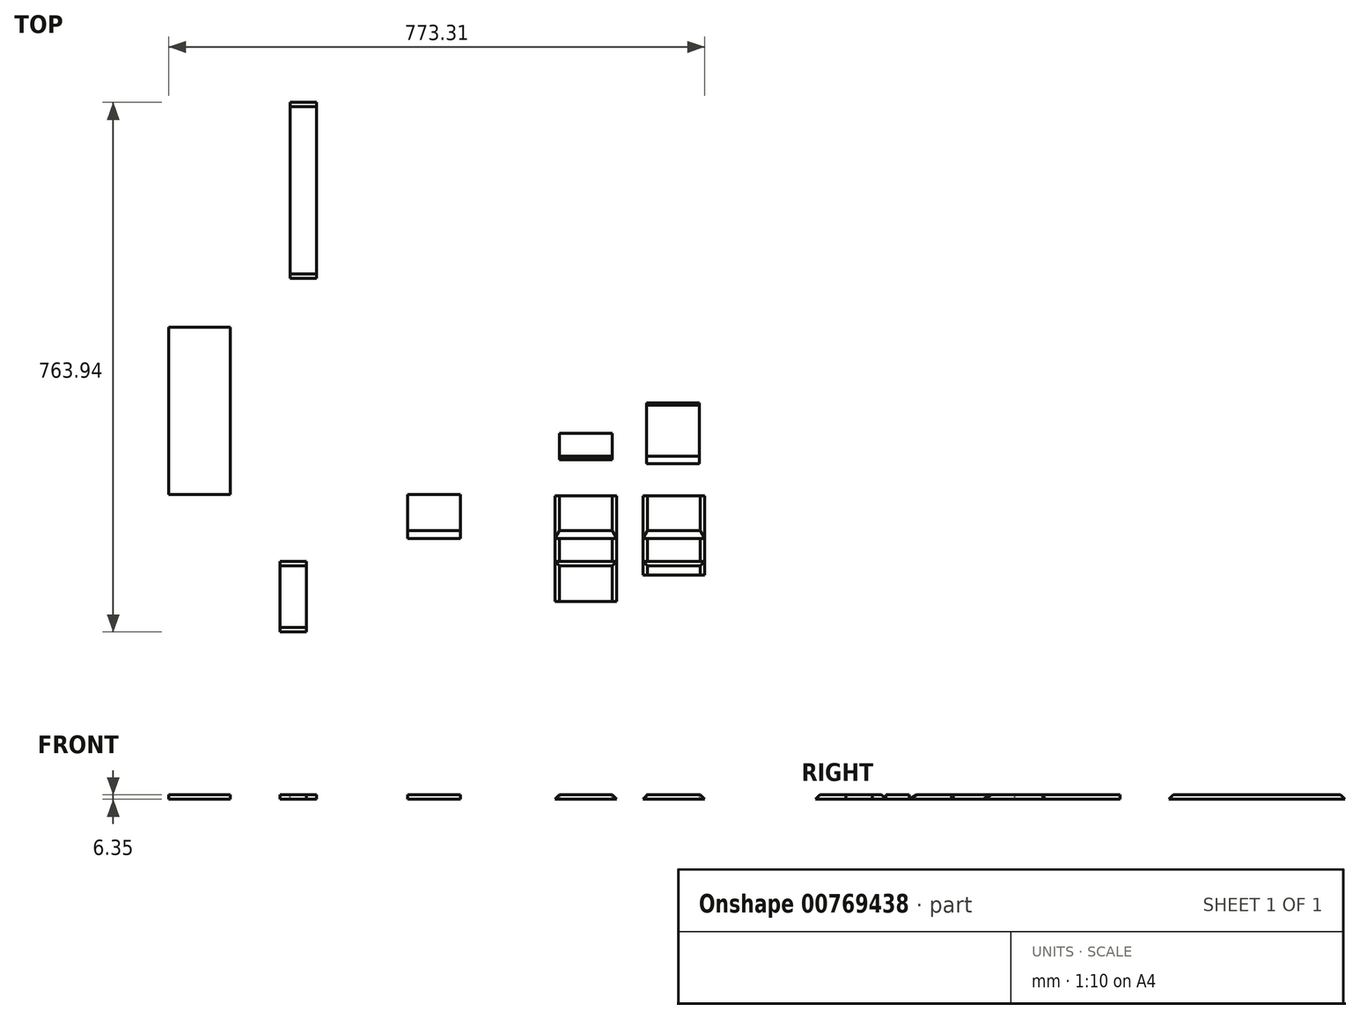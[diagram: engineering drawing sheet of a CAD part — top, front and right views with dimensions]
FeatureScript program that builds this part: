
annotation { "Feature Type Name" : "Feature", "Feature Type Description" : "" }
export const myFeature = defineFeature(function(context is Context, id is Id, definition is map)
    precondition{}
    {
        {
            var Q0;
            Q0=qCreatedBy(makeId("Top.planeOp"),FACE);
            var sketch = newSketch(context, id + "F0", { "sketchPlane" : qUnion([Q0])});
            skLineSegment(sketch, "E0.bottom", {"start": v(44.45, -76.2) * mm, "end": v(-44.45, -76.2) * mm});
            skLineSegment(sketch, "E0.top", {"start": v(44.45, 76.2) * mm, "end": v(-44.45, 76.2) * mm});
            skLineSegment(sketch, "E0.left", {"start": v(44.45, -76.2) * mm, "end": v(44.45, 76.2) * mm});
            skLineSegment(sketch, "E0.right", {"start": v(-44.45, -76.2) * mm, "end": v(-44.45, 76.2) * mm});
            skPoint(sketch, "E0.middle", {"position": v(0, 0) * mm});
            skSolve(sketch);
        }
        {
            var Q0;
            Q0 = qSketchRegion(id + "F0", true);
            extrude(context, id + "F1", {"entities" : qUnion([Q0]), "depth" : 6.35 * mm, "offsetDistance" : 25 * mm});
        }
        {
            var Q0;
            Q0=makeQuery(id+"F1.opExtrude","SWEPT_FACE",FACE,{"disambiguationData":[OSD([sQuery(id+"F0.wireOp",EDGE,"E0.bottom")])]});
            var sketch = newSketch(context, id + "F2", { "sketchPlane" : qUnion([Q0])});
            skLineSegment(sketch, "E1.bottom", {"start": v(44.45, 6.35) * mm, "end": v(38.1, 6.35) * mm});
            skLineSegment(sketch, "E2", {"start": v(44.45, 6.35) * mm, "end": v(44.45, 0) * mm});
            skLineSegment(sketch, "E3", {"start": v(44.45, 0) * mm, "end": v(38.1, 6.35) * mm});
            skLineSegment(sketch, "E4", {"start": v(-44.45, 6.35) * mm, "end": v(-38.1, 6.35) * mm});
            skLineSegment(sketch, "E5", {"start": v(-38.1, 6.35) * mm, "end": v(-44.45, 0) * mm});
            skLineSegment(sketch, "E6", {"start": v(-44.45, 0) * mm, "end": v(-44.45, 6.35) * mm});
            skSolve(sketch);
        }
        {
            var Q0;
            Q0 = qSketchRegion(id + "F2", true);
            extrude(context, id + "F3", {"entities" : qUnion([Q0]), "operationType" : NewBodyOperationType.REMOVE, "endBound" : BoundingType.THROUGH_ALL, "oppositeDirection" : true, "depth" : 25 * mm, "offsetDistance" : 25 * mm});
        }
        {
            var Q0;
            Q0=qCreatedBy(makeId("Top.planeOp"),FACE);
            var sketch = newSketch(context, id + "F4", { "sketchPlane" : qUnion([Q0])});
            skLineSegment(sketch, "E7.bottom", {"start": v(38.1, 128.47) * mm, "end": v(-38.1, 128.47) * mm});
            skLineSegment(sketch, "E7.top", {"start": v(38.1, 166.57) * mm, "end": v(-38.1, 166.57) * mm});
            skLineSegment(sketch, "E7.left", {"start": v(38.1, 128.47) * mm, "end": v(38.1, 166.57) * mm});
            skLineSegment(sketch, "E7.right", {"start": v(-38.1, 128.47) * mm, "end": v(-38.1, 166.57) * mm});
            skPoint(sketch, "E7.middle", {"position": v(0, 147.52) * mm});
            skSolve(sketch);
        }
        {
            var Q0;
            Q0 = qSketchRegion(id + "F4", true);
            extrude(context, id + "F5", {"entities" : qUnion([Q0]), "depth" : 6.35 * mm, "offsetDistance" : 25 * mm});
        }
        {
            var Q0;
            Q0=makeQuery(id+"F5.opExtrude","SWEPT_FACE",FACE,{"disambiguationData":[OSD([sQuery(id+"F4.wireOp",EDGE,"E7.right")])]});
            var sketch = newSketch(context, id + "F6", { "sketchPlane" : qUnion([Q0])});
            skLineSegment(sketch, "E8", {"start": v(-128.47, 0) * mm, "end": v(-132.13, 6.35) * mm});
            skLineSegment(sketch, "E9", {"start": v(-132.13, 6.35) * mm, "end": v(-128.47, 6.35) * mm});
            skLineSegment(sketch, "E10", {"start": v(-128.47, 6.35) * mm, "end": v(-128.47, 0) * mm});
            skSolve(sketch);
        }
        {
            var Q0;
            Q0 = qSketchRegion(id + "F6", true);
            extrude(context, id + "F7", {"entities" : qUnion([Q0]), "operationType" : NewBodyOperationType.REMOVE, "endBound" : BoundingType.THROUGH_ALL, "oppositeDirection" : true, "depth" : 25 * mm, "offsetDistance" : 25 * mm});
        }
        {
            var Q0;
            Q0=makeQuery(id+"F1.opExtrude","SWEPT_BODY",BODY,{"disambiguationData":[OSD([sQuery(id+"F0.wireOp",EDGE,"E0.bottom"),sQuery(id+"F0.wireOp",EDGE,"E0.top"),sQuery(id+"F0.wireOp",EDGE,"E0.left"),sQuery(id+"F0.wireOp",EDGE,"E0.right")])]});
            transform(context, id + "F8", {"entities" : qUnion([Q0]), "transformType" : TransformType.TRANSLATION_3D, "dx" : 127 * mm, "dy" : 0 * mm, "dz" : 0 * mm, "makeCopy" : true});
        }
        {
            var Q0;
            Q0=qCreatedBy(makeId("Top.planeOp"),FACE);
            var sketch = newSketch(context, id + "F9", { "sketchPlane" : qUnion([Q0])});
            skLineSegment(sketch, "E11.bottom", {"start": v(163.93, 122.3) * mm, "end": v(87.73, 122.3) * mm});
            skLineSegment(sketch, "E11.top", {"start": v(163.93, 210.44) * mm, "end": v(87.73, 210.44) * mm});
            skLineSegment(sketch, "E11.left", {"start": v(163.93, 122.3) * mm, "end": v(163.93, 210.44) * mm});
            skLineSegment(sketch, "E11.right", {"start": v(87.73, 122.3) * mm, "end": v(87.73, 210.44) * mm});
            skPoint(sketch, "E11.middle", {"position": v(125.83, 166.37) * mm});
            skSolve(sketch);
        }
        {
            var Q0;
            Q0 = qSketchRegion(id + "F9", true);
            extrude(context, id + "F10", {"entities" : qUnion([Q0]), "depth" : 6.35 * mm, "offsetDistance" : 25.4 * mm});
        }
        {
            var Q0;
            Q0=makeQuery(id+"F10.opExtrude","SWEPT_FACE",FACE,{"disambiguationData":[OSD([sQuery(id+"F9.wireOp",EDGE,"E11.left")])]});
            var sketch = newSketch(context, id + "F11", { "sketchPlane" : qUnion([Q0])});
            skLineSegment(sketch, "E12", {"start": v(122.3, 0) * mm, "end": v(122.3, 6.35) * mm});
            skLineSegment(sketch, "E13", {"start": v(210.44, 0) * mm, "end": v(206.78, 6.35) * mm});
            skLineSegment(sketch, "E14", {"start": v(206.78, 6.35) * mm, "end": v(210.44, 6.35) * mm});
            skLineSegment(sketch, "E15", {"start": v(210.44, 6.35) * mm, "end": v(210.44, 0) * mm});
            skLineSegment(sketch, "E16", {"start": v(122.3, 6.35) * mm, "end": v(133.3, 6.35) * mm});
            skLineSegment(sketch, "E17", {"start": v(133.3, 6.35) * mm, "end": v(122.3, 0) * mm});
            skSolve(sketch);
        }
        {
            var Q0;
            Q0 = qSketchRegion(id + "F11", true);
            extrude(context, id + "F12", {"entities" : qUnion([Q0]), "operationType" : NewBodyOperationType.REMOVE, "endBound" : BoundingType.THROUGH_ALL, "oppositeDirection" : true, "depth" : 25.4 * mm, "offsetDistance" : 25.4 * mm});
        }
        {
            var Q0;
            Q0=makeQuery(id+"F8.opPattern","COPY",FACE,{"derivedFrom":makeQuery(id+"F1.opExtrude","CAP_FACE",FACE,{"disambiguationData":[OSD([sQuery(id+"F0.wireOp",EDGE,"E0.bottom"),sQuery(id+"F0.wireOp",EDGE,"E0.top"),sQuery(id+"F0.wireOp",EDGE,"E0.left"),sQuery(id+"F0.wireOp",EDGE,"E0.right")])],"isStart":true}),"instanceName":"1"});
            var sketch = newSketch(context, id + "F13", { "sketchPlane" : qUnion([Q0])});
            skLineSegment(sketch, "E18", {"start": v(82.55, 38.1) * mm, "end": v(171.45, 38.1) * mm});
            skLineSegment(sketch, "E19", {"start": v(171.45, 38.1) * mm, "end": v(171.45, 76.2) * mm});
            skLineSegment(sketch, "E20", {"start": v(171.45, 76.2) * mm, "end": v(82.55, 76.2) * mm});
            skLineSegment(sketch, "E21", {"start": v(82.55, 76.2) * mm, "end": v(82.55, 38.1) * mm});
            skSolve(sketch);
        }
        {
            var Q0;
            Q0 = qSketchRegion(id + "F13", true);
            extrude(context, id + "F14", {"entities" : qUnion([Q0]), "operationType" : NewBodyOperationType.REMOVE, "endBound" : BoundingType.THROUGH_ALL, "oppositeDirection" : true, "depth" : 25.4 * mm, "offsetDistance" : 25.4 * mm});
        }
        {
            var Q0;
            Q0=qCreatedBy(makeId("Top.planeOp"),FACE);
            var sketch = newSketch(context, id + "F15", { "sketchPlane" : qUnion([Q0])});
            skLineSegment(sketch, "E22.bottom", {"start": v(-180.64, 14.82) * mm, "end": v(-256.84, 14.82) * mm});
            skLineSegment(sketch, "E22.top", {"start": v(-180.64, 78.32) * mm, "end": v(-256.84, 78.32) * mm});
            skLineSegment(sketch, "E22.left", {"start": v(-180.64, 14.82) * mm, "end": v(-180.64, 78.32) * mm});
            skLineSegment(sketch, "E22.right", {"start": v(-256.84, 14.82) * mm, "end": v(-256.84, 78.32) * mm});
            skPoint(sketch, "E22.middle", {"position": v(-218.74, 46.57) * mm});
            skSolve(sketch);
        }
        {
            var Q0;
            Q0 = qSketchRegion(id + "F15", true);
            extrude(context, id + "F16", {"entities" : qUnion([Q0]), "depth" : 6.35 * mm, "offsetDistance" : 25.4 * mm});
        }
        {
            var Q0;
            Q0=makeQuery(id+"F16.opExtrude","SWEPT_FACE",FACE,{"disambiguationData":[OSD([sQuery(id+"F15.wireOp",EDGE,"E22.right")])]});
            var sketch = newSketch(context, id + "F17", { "sketchPlane" : qUnion([Q0])});
            skLineSegment(sketch, "E23", {"start": v(-14.82, 0) * mm, "end": v(-25.82, 6.35) * mm});
            skLineSegment(sketch, "E24", {"start": v(-25.82, 6.35) * mm, "end": v(-14.82, 6.35) * mm});
            skLineSegment(sketch, "E25", {"start": v(-14.82, 6.35) * mm, "end": v(-14.82, 0) * mm});
            skSolve(sketch);
        }
        {
            var Q0;
            Q0 = qSketchRegion(id + "F17", true);
            extrude(context, id + "F18", {"entities" : qUnion([Q0]), "operationType" : NewBodyOperationType.REMOVE, "endBound" : BoundingType.THROUGH_ALL, "oppositeDirection" : true, "depth" : 25.4 * mm, "offsetDistance" : 25.4 * mm});
        }
        {
            var Q0;
            Q0=qCreatedBy(makeId("Top.planeOp"),FACE);
            var sketch = newSketch(context, id + "F19", { "sketchPlane" : qUnion([Q0])});
            skLineSegment(sketch, "E26.bottom", {"start": v(-512.96, 77.97) * mm, "end": v(-601.86, 77.97) * mm});
            skLineSegment(sketch, "E26.top", {"start": v(-512.96, 319.27) * mm, "end": v(-601.86, 319.27) * mm});
            skLineSegment(sketch, "E26.left", {"start": v(-512.96, 77.97) * mm, "end": v(-512.96, 319.27) * mm});
            skLineSegment(sketch, "E26.right", {"start": v(-601.86, 77.97) * mm, "end": v(-601.86, 319.27) * mm});
            skPoint(sketch, "E26.middle", {"position": v(-557.41, 198.62) * mm});
            skSolve(sketch);
        }
        {
            var Q0;
            Q0 = qSketchRegion(id + "F19", true);
            extrude(context, id + "F20", {"entities" : qUnion([Q0]), "depth" : 6.35 * mm, "offsetDistance" : 25.4 * mm});
        }
        {
            var Q0;
            Q0=qCreatedBy(makeId("Top.planeOp"),FACE);
            var sketch = newSketch(context, id + "F21", { "sketchPlane" : qUnion([Q0])});
            skLineSegment(sketch, "E27.bottom", {"start": v(-388.68, 389.65) * mm, "end": v(-426.78, 389.65) * mm});
            skLineSegment(sketch, "E27.top", {"start": v(-388.68, 643.65) * mm, "end": v(-426.78, 643.65) * mm});
            skLineSegment(sketch, "E27.left", {"start": v(-388.68, 389.65) * mm, "end": v(-388.68, 643.65) * mm});
            skLineSegment(sketch, "E27.right", {"start": v(-426.78, 389.65) * mm, "end": v(-426.78, 643.65) * mm});
            skPoint(sketch, "E27.middle", {"position": v(-407.73, 516.65) * mm});
            skSolve(sketch);
        }
        {
            var Q0;
            Q0 = qSketchRegion(id + "F21", true);
            extrude(context, id + "F22", {"entities" : qUnion([Q0]), "depth" : 6.35 * mm, "offsetDistance" : 25.4 * mm});
        }
        {
            var Q0;
            Q0=makeQuery(id+"F22.opExtrude","SWEPT_FACE",FACE,{"disambiguationData":[OSD([sQuery(id+"F21.wireOp",EDGE,"E27.right")])]});
            var sketch = newSketch(context, id + "F23", { "sketchPlane" : qUnion([Q0])});
            skLineSegment(sketch, "E28", {"start": v(-643.65, 0) * mm, "end": v(-637.3, 6.35) * mm});
            skLineSegment(sketch, "E29", {"start": v(-637.3, 6.35) * mm, "end": v(-643.65, 6.35) * mm});
            skLineSegment(sketch, "E30", {"start": v(-643.65, 6.35) * mm, "end": v(-643.65, 0) * mm});
            skLineSegment(sketch, "E31", {"start": v(-389.65, 0) * mm, "end": v(-396, 6.35) * mm});
            skLineSegment(sketch, "E32", {"start": v(-396, 6.35) * mm, "end": v(-389.65, 6.35) * mm});
            skLineSegment(sketch, "E33", {"start": v(-389.65, 6.35) * mm, "end": v(-389.65, 0) * mm});
            skSolve(sketch);
        }
        {
            var Q0;
            Q0 = qSketchRegion(id + "F23", true);
            extrude(context, id + "F24", {"entities" : qUnion([Q0]), "operationType" : NewBodyOperationType.REMOVE, "endBound" : BoundingType.THROUGH_ALL, "oppositeDirection" : true, "depth" : 25.4 * mm, "offsetDistance" : 25.4 * mm});
        }
        {
            var Q0;
            Q0=qCreatedBy(makeId("Top.planeOp"),FACE);
            var sketch = newSketch(context, id + "F25", { "sketchPlane" : qUnion([Q0])});
            skLineSegment(sketch, "E34.bottom", {"start": v(-441.15, -120.3) * mm, "end": v(-403.05, -120.3) * mm});
            skLineSegment(sketch, "E34.top", {"start": v(-441.15, -18.7) * mm, "end": v(-403.05, -18.7) * mm});
            skLineSegment(sketch, "E34.left", {"start": v(-441.15, -120.3) * mm, "end": v(-441.15, -18.7) * mm});
            skLineSegment(sketch, "E34.right", {"start": v(-403.05, -120.3) * mm, "end": v(-403.05, -18.7) * mm});
            skPoint(sketch, "E34.middle", {"position": v(-422.1, -69.5) * mm});
            skSolve(sketch);
        }
        {
            var Q0;
            Q0 = qSketchRegion(id + "F25", true);
            extrude(context, id + "F26", {"entities" : qUnion([Q0]), "depth" : 6.35 * mm, "offsetDistance" : 25.4 * mm});
        }
        {
            var Q0;
            Q0=makeQuery(id+"F26.opExtrude","SWEPT_FACE",FACE,{"disambiguationData":[OSD([sQuery(id+"F25.wireOp",EDGE,"E34.left")])]});
            var sketch = newSketch(context, id + "F27", { "sketchPlane" : qUnion([Q0])});
            skLineSegment(sketch, "E35", {"start": v(18.7, 0) * mm, "end": v(25.04, 6.35) * mm});
            skLineSegment(sketch, "E36", {"start": v(25.04, 6.35) * mm, "end": v(18.7, 6.35) * mm});
            skLineSegment(sketch, "E37", {"start": v(18.7, 6.35) * mm, "end": v(18.7, 0) * mm});
            skLineSegment(sketch, "E38", {"start": v(120.3, 0) * mm, "end": v(113.94, 6.35) * mm});
            skLineSegment(sketch, "E39", {"start": v(113.94, 6.35) * mm, "end": v(120.3, 6.35) * mm});
            skLineSegment(sketch, "E40", {"start": v(120.3, 6.35) * mm, "end": v(120.3, 0) * mm});
            skSolve(sketch);
        }
        {
            var Q0;
            Q0 = qSketchRegion(id + "F27", true);
            extrude(context, id + "F28", {"entities" : qUnion([Q0]), "operationType" : NewBodyOperationType.REMOVE, "endBound" : BoundingType.THROUGH_ALL, "oppositeDirection" : true, "depth" : 25.4 * mm, "offsetDistance" : 25.4 * mm});
        }
    });
